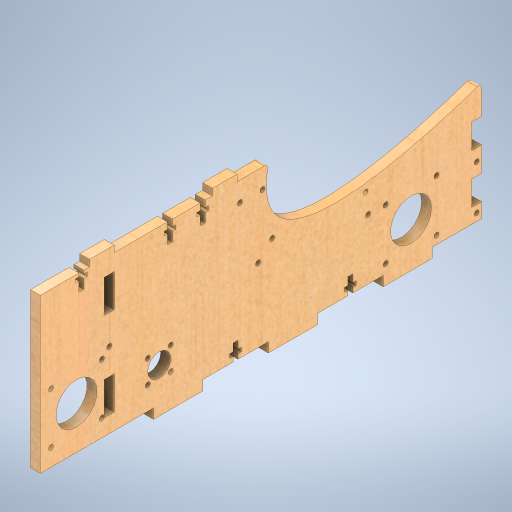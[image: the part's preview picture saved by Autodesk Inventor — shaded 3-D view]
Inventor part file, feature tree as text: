
AUTODESK INVENTOR PART (.ipt)
format: ipt  version: 2024.2 (Build 282272000, 272)  size: 738,816 bytes
history: native  units: mm
features: extrude x14, sketch x14, other x4, fillet x1, reference x1
ambient origin geometry x8: Origin, YZ Plane, XZ Plane, XY Plane, X Axis, Y Axis, Z Axis, Center Point
bodies: Body1 (feature_tree)
feature tree (34):
  other  "Твердое тело1"
  extrude  "Выдавливание1"  Depth=230.0mm
  extrude  "Выдавливание2"  Depth=100.0mm
  extrude  "Выдавливание3"  Depth=6.0mm TaperAngle=0.0deg
  extrude  "Выдавливание4"  Depth=30.0mm
  extrude  "Выдавливание5"  Depth=30.0mm
  extrude  "Выдавливание6"  Depth=40.0mm
  extrude  "Выдавливание7"  Depth=30.0mm
  extrude  "Выдавливание8"  Depth=30.0mm
  extrude  "Выдавливание9"  Depth=40.0mm
  fillet  "Сопряжение1"  [1 undecoded]
  extrude  "Выдавливание11"  Depth=6.0mm
  extrude  "Выдавливание12"  Depth=6.0mm
  extrude  "Выдавливание13"  Depth=10.0mm
  extrude  "Выдавливание14"  Depth=10.0mm
  extrude  "Выдавливание10"  Depth=20.0mm
  sketch  "Эскиз1"
  sketch  "Эскиз2"
  sketch  "Эскиз3"
  sketch  "Эскиз4"
  sketch  "Эскиз5"
  sketch  "Эскиз6"
  sketch  "Эскиз7"
  sketch  "Эскиз8"
  sketch  "Эскиз9"
  sketch  "Эскиз10"
  sketch  "Эскиз11"
  sketch  "Эскиз12"
  reference  "Ссылка1"
  sketch  "Эскиз13"
  sketch  "Эскиз14"
  other  "<userpath>\Documents\Artist-v2\3D\Робот.iam"
  other  "Робот.iam"
  other  "крышка:1"
note: 1 required parameter value undecoded (feature->parameter linkage not recoverable at this tier; creation-order binding heuristic only, values carry confidence <= 0.55)
